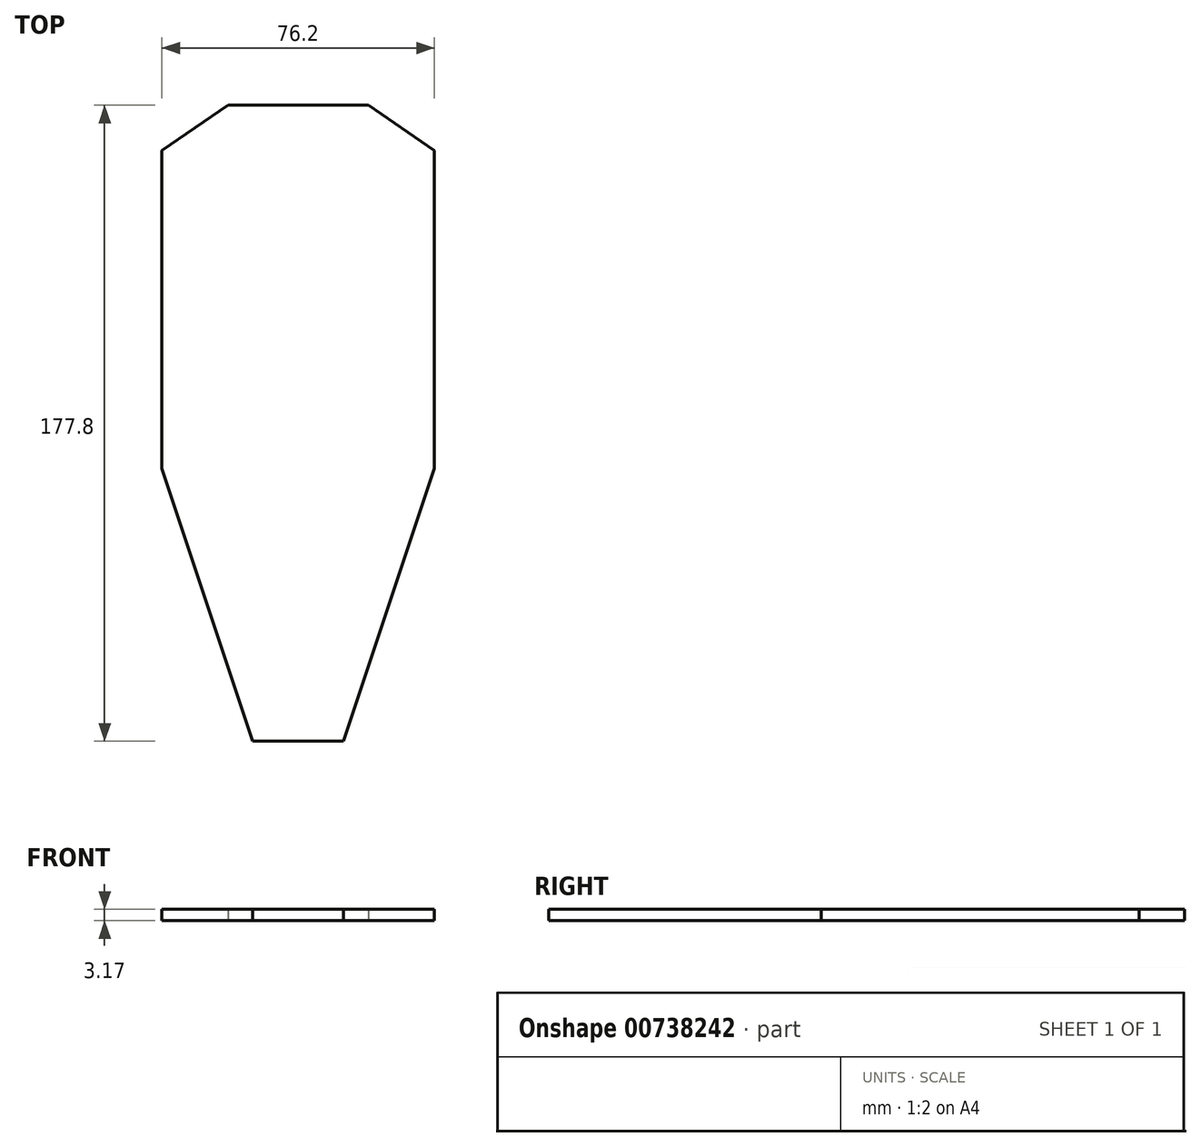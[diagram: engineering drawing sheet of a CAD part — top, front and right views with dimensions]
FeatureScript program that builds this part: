
annotation { "Feature Type Name" : "Feature", "Feature Type Description" : "" }
export const myFeature = defineFeature(function(context is Context, id is Id, definition is map)
    precondition{}
    {
        {
            var Q0;
            Q0=qCreatedBy(makeId("Top.planeOp"),FACE);
            var sketch = newSketch(context, id + "F0", { "sketchPlane" : qUnion([Q0])});
            skLineSegment(sketch, "E0.0.2", {"start": v(19.45, 101.6) * mm, "end": v(37.93, 88.9) * mm});
            skLineSegment(sketch, "E0.0.3", {"start": v(37.93, 88.9) * mm, "end": v(37.93, 0) * mm});
            skLineSegment(sketch, "E0.0.4", {"start": v(37.93, 0) * mm, "end": v(12.53, -76.2) * mm});
            skLineSegment(sketch, "E0.0.5", {"start": v(12.53, -76.2) * mm, "end": v(-12.87, -76.2) * mm});
            skLineSegment(sketch, "E0.0.6", {"start": v(-12.87, -76.2) * mm, "end": v(-38.27, 0) * mm});
            skLineSegment(sketch, "E0.0.7", {"start": v(-38.27, 0) * mm, "end": v(-38.27, 88.9) * mm});
            skLineSegment(sketch, "E0.0.8", {"start": v(-38.27, 88.9) * mm, "end": v(-19.78, 101.6) * mm});
            skLineSegment(sketch, "E1", {"start": v(19.45, 101.6) * mm, "end": v(-19.78, 101.6) * mm});
            skSolve(sketch);
        }
        {
            var Q0;
            Q0=makeQuery(id+"F0.imprint","IMPRINT",FACE,{"disambiguationData":[TD([[makeQuery(id+"F0.imprint","IMPRINT",EDGE,{"derivedFrom":sQuery(id+"F0.wireOp",EDGE,"E0.0.2")}),-1.0]])]});
            extrude(context, id + "F1", {"entities" : qUnion([Q0]), "depth" : 3.17 * mm, "offsetDistance" : 25.4 * mm});
        }
    });
